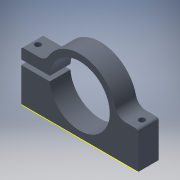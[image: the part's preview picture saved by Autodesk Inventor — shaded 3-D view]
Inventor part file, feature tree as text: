
AUTODESK INVENTOR PART (.ipt)
format: ipt  version: 2017 (Build 210142000, 142)  size: 146,944 bytes
history: native  units: in
note: dims shown in document units (in); Inventor stores cm internally (conversion verified against a paired STEP export)
features: other x7, sketch x1
ambient origin geometry x8: Origin, YZ Plane, XZ Plane, XY Plane, X Axis, Y Axis, Z Axis, Center Point
bodies: Solid1 (feature_tree)
feature tree (8):
  other  "tetrix_739089_2012"
  other  "A_2"
  other  "A_3"
  other  "A_4"
  other  "FRONT"
  other  "TOP"
  other  "RIGHT"
  sketch  "Sketch1"
